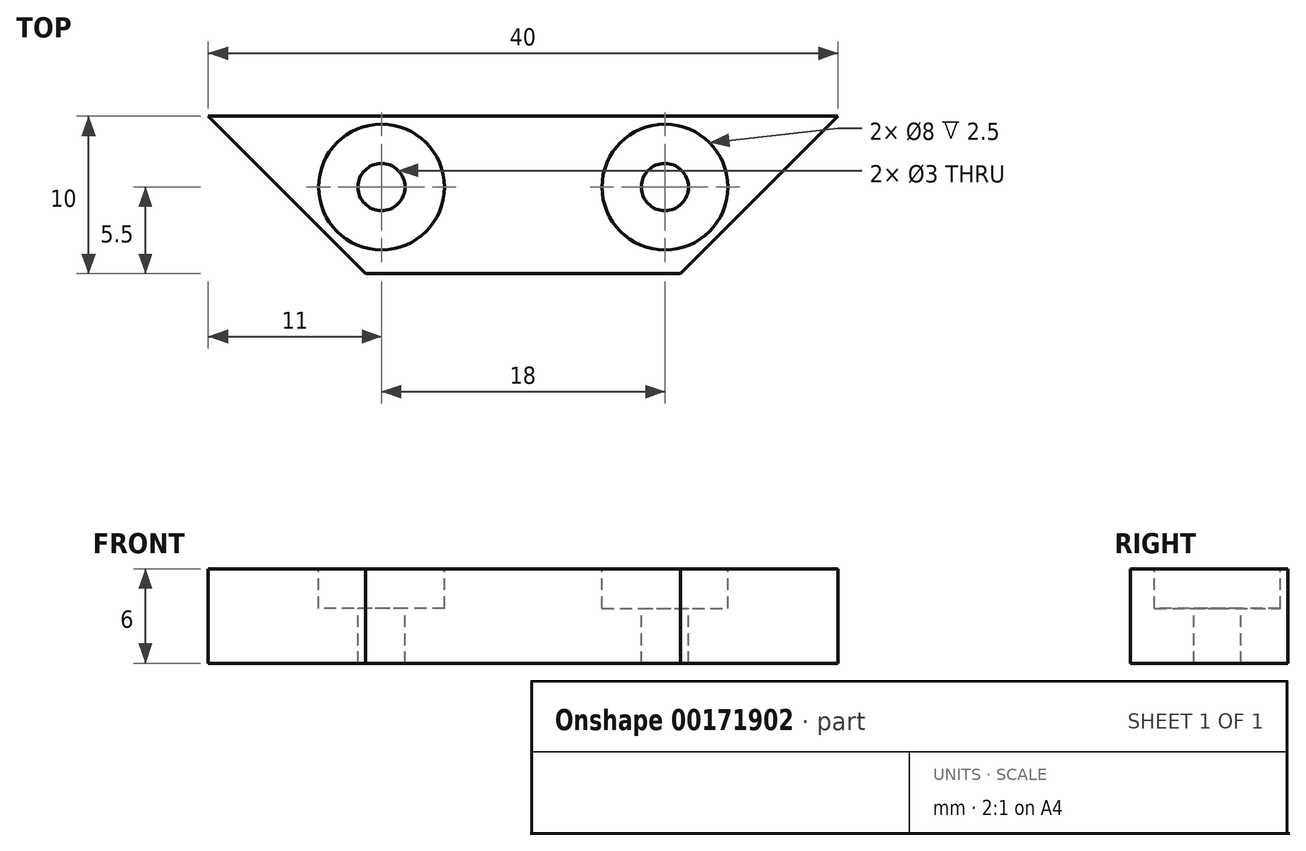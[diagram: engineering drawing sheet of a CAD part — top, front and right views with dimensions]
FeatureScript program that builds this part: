
annotation { "Feature Type Name" : "Feature", "Feature Type Description" : "" }
export const myFeature = defineFeature(function(context is Context, id is Id, definition is map)
    precondition{}
    {
        {
            var Q0;
            Q0=qCreatedBy(makeId("Top.planeOp"),FACE);
            var sketch = newSketch(context, id + "F0", { "sketchPlane" : qUnion([Q0])});
            skLineSegment(sketch, "E0.bottom", {"start": v(0, -5) * mm, "end": v(-20, -5) * mm});
            skLineSegment(sketch, "E0.top", {"start": v(0, 5) * mm, "end": v(-20, 5) * mm});
            skLineSegment(sketch, "E0.right", {"start": v(-20, -5) * mm, "end": v(-20, 5) * mm});
            skPoint(sketch, "E0.middle", {"position": v(0, 0) * mm});
            skLineSegment(sketch, "E1", {"start": v(0, 9.73) * mm, "end": v(0, -12.17) * mm});
            skPoint(sketch, "E0.left.end.orphan", {"position": v(20, 5) * mm});
            skPoint(sketch, "E0.left.start.orphan", {"position": v(20, -5) * mm});
            skSolve(sketch);
        }
        {
            var Q0;
            Q0 = qSketchRegion(id + "F0", true);
            extrude(context, id + "F1", {"entities" : qUnion([Q0]), "depth" : 6 * mm});
        }
        {
            var Q0;
            Q0=makeQuery(id+"F1.opExtrude","SWEPT_EDGE",EDGE,{"disambiguationData":[OSD([sQuery(id+"F0.wireOp",EDGE,"E0.bottom"),sQuery(id+"F0.wireOp",EDGE,"E0.right")])]});
            chamfer(context, id + "F2", {"entities" : qUnion([Q0]), "width" : 10 * mm, "tangentPropagation" : true});
        }
        {
            var Q0;
            Q0=makeQuery(id+"F1.opExtrude","CAP_FACE",FACE,{"disambiguationData":[OSD([sQuery(id+"F0.wireOp",EDGE,"E0.bottom"),sQuery(id+"F0.wireOp",EDGE,"E0.top"),sQuery(id+"F0.wireOp",EDGE,"E0.left"),sQuery(id+"F0.wireOp",EDGE,"E0.right")])],"isStart":false});
            var sketch = newSketch(context, id + "F3", { "sketchPlane" : qUnion([Q0])});
            skCircle(sketch, "E2", {"center": v(-9, 0.5) * mm, "radius": 4 * mm});
            skSolve(sketch);
        }
        {
            var Q0;
            Q0 = qSketchRegion(id + "F3", true);
            extrude(context, id + "F4", {"entities" : qUnion([Q0]), "operationType" : NewBodyOperationType.REMOVE, "oppositeDirection" : true, "depth" : 2.5 * mm});
        }
        {
            var Q0;
            Q0=makeQuery(id+"F4.boolean.opBoolean","COPY",FACE,{"derivedFrom":makeQuery(id+"F4.opExtrude","CAP_FACE",FACE,{"disambiguationData":[OSD([sQuery(id+"F3.wireOp",EDGE,"E2")])],"isStart":false})});
            var sketch = newSketch(context, id + "F5", { "sketchPlane" : qUnion([Q0])});
            skCircle(sketch, "E3", {"center": v(-9, 0.5) * mm, "radius": 1.28 * mm});
            skSolve(sketch);
        }
        {
            var Q0;
            Q0=sQuery(id+"F5.wireOp",VERTEX,"E3.center");
            var Q1;
            Q1=makeQuery(id+"F1.opExtrude","SWEPT_BODY",BODY,{"disambiguationData":[OSD([sQuery(id+"F0.wireOp",EDGE,"E0.bottom"),sQuery(id+"F0.wireOp",EDGE,"E0.top"),sQuery(id+"F0.wireOp",EDGE,"E0.left"),sQuery(id+"F0.wireOp",EDGE,"E0.right")])]});
            hole(context, id + "F6", {"style" : HoleStyle.C_BORE, "endStyle" : HoleEndStyle.BLIND, "holeDiameter" : 3 * mm, "cBoreDiameter" : 3 * mm, "cBoreDepth" : 10 * mm, "holeDepth" : 10 * mm, "tappedDepth" : 12 * mm, "tapClearance" : 3, "locations" : qUnion([Q0]), "scope" : qUnion([Q1])});
        }
        {
            var Q0;
            Q0=makeQuery(id+"F1.opExtrude","SWEPT_BODY",BODY,{"disambiguationData":[OSD([sQuery(id+"F0.wireOp",EDGE,"E0.bottom"),sQuery(id+"F0.wireOp",EDGE,"E0.top"),sQuery(id+"F0.wireOp",EDGE,"E0.right"),sQuery(id+"F0.wireOp",EDGE,"E1")])]});
            var Q1;
            Q1=qCreatedBy(makeId("Right.planeOp"),FACE);
            mirror(context, id + "F7", {"operationType" : NewBodyOperationType.ADD, "entities" : qUnion([Q0]), "mirrorPlane" : qUnion([Q1])});
        }
    });
